# Revit family: IS_ConnectFreedom_E8242_BIM_DE
name_source: partatom
category: Plumbing Fixtures
revit_build: Autodesk Revit MEP 2015 (Build: 20140606_1530(x64)
units: mm (PartAtom-declared; Revit-internal decimal feet)

## types (1)
- E824201 - CONNECT FREEDOM XL seat retaining buffers
    Assembly Code = C1030204
    BIMobject category = Toilet Seats
    BOSUseNativeGeometries = 1
    Brand url = http://www.idealstandard.co.uk
    Description = E824201 CONNECT FREEDOM XL seat retaining buffers
    DrainSize = 0 mm  [stored 0 ft]
    EAN code = 5017830471219
    Edition number = 1
    FlushRate = 0 m³
    FlushingRate = 0
    IFC Classification = Sanitary Terminal
    IfcExportType = SEAT&COVER
    InletConnectionSize = 0 mm  [stored 0 ft]
    Installation instructions = http://www.idealstandard.de
    Manufacturer name = Ideal Standard
    ManufacturerURL = www.idealstandard.com
    Material = Duroplast
    Material main = Plastic
    MaterialThickness = 0 mm  [stored 0 ft]
    Model = E824201
    ModelNumber = E824201
    ModelReference = E824201
    Name = CONNECT FREEDOM XL seat retaining buffers
    NettWeight = 2,1 kg
    Nominal height = 43
    Nominal width = 444
    NominalDepth = 480 mm  [stored 1.5748 ft]
    NominalHeight = 43 mm  [stored 0.141076 ft]
    NominalLength = 480 mm  [stored 1.5748 ft]
    NominalWidth = 444 mm  [stored 1.45669 ft]
    OmniClass Code = 23-31 19 19 17
    OmniClass Description = Water Closet Seats
    OutletConnectionSize = 0 mm  [stored 0 ft]
    Product Guid = 1f33a07b-b55e-4cf0-bd63-5bb60ffaa9d6
    Product SKU = E8242
    Product data url = https://bimobject.com
    Product family = CONNECT FREEDOM
    Product group = WC seats
    Product name = CONNECT FREEDOM XL seat retaining buffers
    Product url = http://www.idealstandard.de
    ProductInformation = www.idealstandard.de/produkte
    QR code = http://bimobject.com
    SeatColor = White
    SeatHasCover = No
    SeatMaterial = Duroplast
    Shape = Sculptured
    Size = 43x480x444
    Space = Internal
    SpareParts = www.idealstandard.de/ersatzteile
    Technical description = E824201 CONNECT FREEDOM XL seat retaining buffers
    URL = www.idealstandard.com
    Uniclass 2015 Code = Pr_40_20_93_95
    Uniclass 2015 Name = WC seats and covers
    Uniclass2015Code = Pr_40_20_93_95
    Uniclass2015Title = WC seats and covers
    Version = 1
    VolumeUnits = Litres
    Weight Net (Kg) = 2.1

note: [stored X ft] marks values corroborated as IEEE doubles in the binary element streams (Revit-internal decimal feet)

## geometry (parser evidence)
native form markers: Blend x4, Sweep x1
no freeform markers — native parametric forms only
